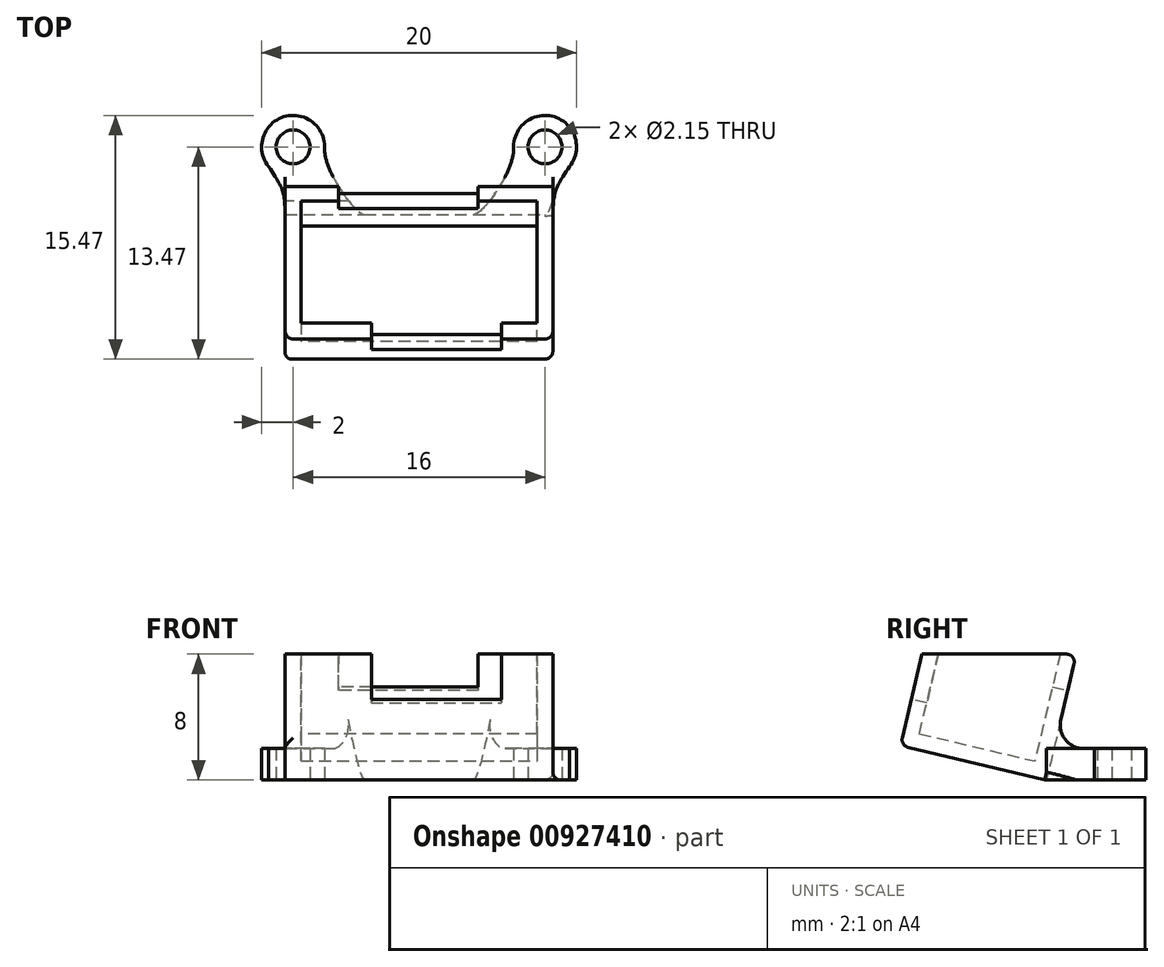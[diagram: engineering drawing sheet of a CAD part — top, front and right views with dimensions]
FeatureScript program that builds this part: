
annotation { "Feature Type Name" : "Feature", "Feature Type Description" : "" }
export const myFeature = defineFeature(function(context is Context, id is Id, definition is map)
    precondition{}
    {
        {
            assignVariable(context, id + "F0", {"name" : "HolderThickness", "anyValue" : 1 * mm});
        }
        {
            assignVariable(context, id + "F1", {"name" : "SpacerThickness", "anyValue" : 2 * mm});
        }
        {
            var Q0;
            Q0=qCreatedBy(makeId("Top.planeOp"),FACE);
            cPlane(context, id + "F2", {"entities" : qUnion([Q0]), "cplaneType" : CPlaneType.OFFSET, "offset" : 15 * mm, "oppositeDirection" : true, "width" : 150 * mm, "height" : 150 * mm});
        }
        {
            var Q0;
            Q0=qCreatedBy(id+"F2.planeOp",FACE);
            cPlane(context, id + "F3", {"entities" : qUnion([Q0]), "cplaneType" : CPlaneType.OFFSET, "offset" : 8 * mm, "width" : 150 * mm, "height" : 150 * mm});
        }
        {
            var Q0;
            Q0=qCreatedBy(id+"F2.planeOp",FACE);
            var sketch = newSketch(context, id + "F4", { "sketchPlane" : qUnion([Q0])});
            skLineSegment(sketch, "E0.bottom", {"start": v(-8.5, -4.3) * mm, "end": v(8.5, -4.3) * mm});
            skLineSegment(sketch, "E0.top", {"start": v(-8.5, -14.1) * mm, "end": v(8.5, -14.1) * mm});
            skLineSegment(sketch, "E0.left", {"start": v(-8.5, -4.3) * mm, "end": v(-8.5, -14.1) * mm});
            skLineSegment(sketch, "E0.right", {"start": v(8.5, -4.3) * mm, "end": v(8.5, -14.1) * mm});
            skPoint(sketch, "E1", {"position": v(0, -4.3) * mm});
            skSolve(sketch);
        }
        {
            var Q0;
            Q0=qCreatedBy(id+"F3.planeOp",FACE);
            var sketch = newSketch(context, id + "F5", { "sketchPlane" : qUnion([Q0])});
            skLineSegment(sketch, "E2.bottom", {"start": v(-8.5, -2.4) * mm, "end": v(8.5, -2.4) * mm});
            skLineSegment(sketch, "E2.top", {"start": v(-8.5, -12.2) * mm, "end": v(8.5, -12.2) * mm});
            skLineSegment(sketch, "E2.left", {"start": v(-8.5, -2.4) * mm, "end": v(-8.5, -12.2) * mm});
            skLineSegment(sketch, "E2.right", {"start": v(8.5, -2.4) * mm, "end": v(8.5, -12.2) * mm});
            skSolve(sketch);
        }
        {
            var Q0;
            Q0=qSketchRegion(id+"F5",true);
            var Q1;
            Q1=qSketchRegion(id+"F4",true);
            loft(context, id + "F6", {"sheetProfilesArray" : [{ "sheetProfileEntities" : qUnion([Q0]) }, { "sheetProfileEntities" : qUnion([Q1]) }]});
        }
        {
            var Q0;
            Q0=makeQuery(id+"F6.opLoft","SWEPT_FACE",FACE,{"disambiguationData":[OSD([sQuery(id+"F4.wireOp",EDGE,"E0.bottom"),sQuery(id+"F4.wireOp",EDGE,"E0.top"),sQuery(id+"F4.wireOp",EDGE,"E0.left"),sQuery(id+"F5.wireOp",EDGE,"E2.bottom"),sQuery(id+"F5.wireOp",EDGE,"E2.top"),sQuery(id+"F5.wireOp",EDGE,"E2.left")])]});
            var sketch = newSketch(context, id + "F7", { "sketchPlane" : qUnion([Q0])});
            skLineSegment(sketch, "E3", {"start": v(4.3, -15) * mm, "end": v(4.07, -14.03) * mm, "construction": true});
            skLineSegment(sketch, "E4", {"start": v(4.3, -15) * mm, "end": v(14.29, -12.63) * mm});
            skLineSegment(sketch, "E5", {"start": v(14.29, -12.63) * mm, "end": v(15.54, -17.9) * mm});
            skLineSegment(sketch, "E6", {"start": v(15.54, -17.9) * mm, "end": v(6.25, -20.1) * mm});
            skLineSegment(sketch, "E7", {"start": v(6.25, -20.1) * mm, "end": v(4.3, -15) * mm});
            skSolve(sketch);
        }
        {
            var Q0;
            Q0=qSketchRegion(id+"F7",true);
            extrude(context, id + "F8", {"entities" : qUnion([Q0]), "operationType" : NewBodyOperationType.REMOVE, "oppositeDirection" : true, "depth" : 25 * mm, "offsetDistance" : 25 * mm});
        }
        {
            var Q0;
            Q0=makeQuery(id+"F6.opLoft","CAP_FACE",FACE,{"disambiguationData":[OSD([makeQuery(id+"F5.imprint","IMPRINT",FACE,{"disambiguationData":[TD([[makeQuery(id+"F5.imprint","IMPRINT",EDGE,{"derivedFrom":sQuery(id+"F5.wireOp",EDGE,"E2.bottom")}),-1.0]])]})])],"isStart":true});
            shell(context, id + "F9", {"entities" : qUnion([Q0]), "thickness" : 1 * mm});
        }
        {
            var Q0;
            Q0=makeQuery(id+"F6.opLoft","SWEPT_FACE",FACE,{"disambiguationData":[OSD([sQuery(id+"F4.wireOp",EDGE,"E0.top"),sQuery(id+"F4.wireOp",EDGE,"E0.left"),sQuery(id+"F4.wireOp",EDGE,"E0.right"),sQuery(id+"F5.wireOp",EDGE,"E2.top"),sQuery(id+"F5.wireOp",EDGE,"E2.left"),sQuery(id+"F5.wireOp",EDGE,"E2.right")])]});
            var sketch = newSketch(context, id + "F10", { "sketchPlane" : qUnion([Q0])});
            skPoint(sketch, "E8.0", {"position": v(-7.5, -14.59) * mm});
            skPoint(sketch, "E9.0", {"position": v(-7.5, -7.6) * mm});
            skPoint(sketch, "E10.0", {"position": v(7.5, -7.6) * mm});
            skPoint(sketch, "E11.0", {"position": v(7.5, -14.59) * mm});
            skLineSegment(sketch, "E12.bottom", {"start": v(-3.02, -4.34) * mm, "end": v(5.23, -4.34) * mm});
            skLineSegment(sketch, "E12.top", {"start": v(-3.03, -12.59) * mm, "end": v(5.23, -12.59) * mm});
            skLineSegment(sketch, "E12.left", {"start": v(-3.02, -4.34) * mm, "end": v(-3.03, -12.59) * mm});
            skLineSegment(sketch, "E12.right", {"start": v(5.23, -4.34) * mm, "end": v(5.23, -12.59) * mm});
            skSolve(sketch);
        }
        {
            var Q0;
            Q0=qSketchRegion(id+"F10",true);
            extrude(context, id + "F11", {"entities" : qUnion([Q0]), "operationType" : NewBodyOperationType.REMOVE, "oppositeDirection" : true, "depth" : getVariable(context, 'HolderThickness'), "offsetDistance" : 25 * mm});
        }
        {
            var Q0;
            Q0=qCreatedBy(id+"F2.planeOp",FACE);
            var sketch = newSketch(context, id + "F12", { "sketchPlane" : qUnion([Q0])});
            skCircle(sketch, "E13", {"center": v(-8, 0) * mm, "radius": 1.07 * mm});
            skCircle(sketch, "E14", {"center": v(8, 0) * mm, "radius": 1.07 * mm});
            skLineSegment(sketch, "E15", {"start": v(8, 0) * mm, "end": v(-8, 0) * mm, "construction": true});
            skCircle(sketch, "E16", {"center": v(-8, 0) * mm, "radius": 2 * mm});
            skCircle(sketch, "E17", {"center": v(8, 0) * mm, "radius": 2 * mm});
            skPoint(sketch, "E18", {"position": v(-9.07, 0) * mm});
            skFitSpline(sketch, "E19.MirrorCS", {"points": [v(-6, -0.14) * mm, v(-3.48, -4.3) * mm], "startDerivative": vector(0, -4.37) * mm, "endDerivative": vector(1.84, -0.2) * mm});
            skFitSpline(sketch, "E20", {"points": [v(-8.5, -4.3) * mm, v(-9.57, -1.24) * mm], "startDerivative": vector(-0.13, 4.25) * mm, "endDerivative": vector(-2.9, 4.1) * mm});
            skLineSegment(sketch, "E21", {"start": v(0, 3.34) * mm, "end": v(0, -3.34) * mm, "construction": true});
            skPoint(sketch, "E21.startSnap0", {"position": v(0, 0) * mm});
            skFitSpline(sketch, "E22.MirrorCS", {"points": [v(6, -0.14) * mm, v(3.48, -4.3) * mm], "startDerivative": vector(0, -4.37) * mm, "endDerivative": vector(-1.84, -0.2) * mm});
            skFitSpline(sketch, "E23.MirrorCS", {"points": [v(8.5, -4.3) * mm, v(9.57, -1.24) * mm], "startDerivative": vector(0.13, 4.25) * mm, "endDerivative": vector(2.9, 4.1) * mm});
            skLineSegment(sketch, "E24", {"start": v(-3.48, -4.3) * mm, "end": v(-8.5, -4.3) * mm});
            skLineSegment(sketch, "E25.MirrorCS", {"start": v(3.48, -4.3) * mm, "end": v(8.5, -4.3) * mm});
            skSolve(sketch);
        }
        {
            var Q0;
            Q0=makeQuery(id+"F12.imprint","IMPRINT",FACE,{"disambiguationData":[TD([[makeQuery(id+"F12.imprint","IMPRINT",EDGE,{"derivedFrom":sQuery(id+"F12.wireOp",EDGE,"E13")}),-1.0]])]});
            var Q1;
            Q1=makeQuery(id+"F12.imprint","IMPRINT",FACE,{"disambiguationData":[TD([[makeQuery(id+"F12.imprint","IMPRINT",EDGE,{"derivedFrom":sQuery(id+"F12.wireOp",EDGE,"E14")}),-1.0]])]});
            extrude(context, id + "F13", {"entities" : qUnion([Q0, Q1]), "depth" : getVariable(context, 'SpacerThickness'), "offsetDistance" : 25 * mm});
        }
        {
            var Q0;
            {var subQ0=sQuery(id+"F12.wireOp",EDGE,"E19.MirrorCS");Q0=makeQuery(id+"F12.imprint","IMPRINT",FACE,{"disambiguationData":[TD([[makeQuery(id+"F12.imprint","IMPRINT",EDGE,{"derivedFrom":subQ0}),-1.0]])]});}
            var Q1;
            {var subQ0=sQuery(id+"F12.wireOp",EDGE,"E22.MirrorCS");Q1=makeQuery(id+"F12.imprint","IMPRINT",FACE,{"disambiguationData":[TD([[makeQuery(id+"F12.imprint","IMPRINT",EDGE,{"derivedFrom":subQ0}),1.0]])]});}
            extrude(context, id + "F14", {"entities" : qUnion([Q0, Q1]), "operationType" : NewBodyOperationType.ADD, "depth" : 2 * mm, "offsetDistance" : 25 * mm});
        }
        {
            var Q0;
            Q0=makeQuery(id+"F14.boolean.opBoolean","INTERSECT",EDGE,{"derivedFrom":[makeQuery(id+"F6.opLoft","SWEPT_FACE",FACE,{"disambiguationData":[OSD([sQuery(id+"F4.wireOp",EDGE,"E0.bottom"),sQuery(id+"F4.wireOp",EDGE,"E0.left"),sQuery(id+"F4.wireOp",EDGE,"E0.right"),sQuery(id+"F5.wireOp",EDGE,"E2.bottom"),sQuery(id+"F5.wireOp",EDGE,"E2.left"),sQuery(id+"F5.wireOp",EDGE,"E2.right")])]}),makeQuery(id+"F14.opExtrude","CAP_FACE",FACE,{"disambiguationData":[OSD([sQuery(id+"F12.wireOp",EDGE,"E17"),sQuery(id+"F12.wireOp",EDGE,"E22.MirrorCS"),sQuery(id+"F12.wireOp",EDGE,"E23.MirrorCS"),sQuery(id+"F12.wireOp",EDGE,"E25.MirrorCS")])],"isStart":false})]});
            var Q1;
            Q1=makeQuery(id+"F14.boolean.opBoolean","INTERSECT",EDGE,{"derivedFrom":[makeQuery(id+"F6.opLoft","SWEPT_FACE",FACE,{"disambiguationData":[OSD([sQuery(id+"F4.wireOp",EDGE,"E0.bottom"),sQuery(id+"F4.wireOp",EDGE,"E0.left"),sQuery(id+"F4.wireOp",EDGE,"E0.right"),sQuery(id+"F5.wireOp",EDGE,"E2.bottom"),sQuery(id+"F5.wireOp",EDGE,"E2.left"),sQuery(id+"F5.wireOp",EDGE,"E2.right")])]}),makeQuery(id+"F14.opExtrude","CAP_FACE",FACE,{"disambiguationData":[OSD([sQuery(id+"F12.wireOp",EDGE,"E16"),sQuery(id+"F12.wireOp",EDGE,"E19.MirrorCS"),sQuery(id+"F12.wireOp",EDGE,"E20"),sQuery(id+"F12.wireOp",EDGE,"E24")])],"isStart":false})]});
            fillet(context, id + "F15", {"entities" : qUnion([Q0, Q1]), "radius" : 1.5 * mm, "tangentPropagation" : true, "allowEdgeOverflow" : false});
        }
        {
            var Q0;
            Q0=makeQuery(id+"F13.boolean.opBoolean","INTERSECT",EDGE,{"derivedFrom":[makeQuery(id+"F6.opLoft","SWEPT_FACE",FACE,{"disambiguationData":[OSD([sQuery(id+"F4.wireOp",EDGE,"E0.bottom"),sQuery(id+"F4.wireOp",EDGE,"E0.top"),sQuery(id+"F4.wireOp",EDGE,"E0.right"),sQuery(id+"F5.wireOp",EDGE,"E2.bottom"),sQuery(id+"F5.wireOp",EDGE,"E2.top"),sQuery(id+"F5.wireOp",EDGE,"E2.right")])]}),makeQuery(id+"F13.opExtrude","CAP_FACE",FACE,{"disambiguationData":[OSD([sQuery(id+"F12.wireOp",EDGE,"E14"),sQuery(id+"F12.wireOp",EDGE,"E17"),sQuery(id+"F12.wireOp",EDGE,"E22.MirrorCS"),sQuery(id+"F12.wireOp",EDGE,"E23.MirrorCS"),sQuery(id+"F12.wireOp",EDGE,"E25.MirrorCS")])],"isStart":false})]});
            var Q1;
            Q1=makeQuery(id+"F13.boolean.opBoolean","INTERSECT",EDGE,{"derivedFrom":[makeQuery(id+"F6.opLoft","SWEPT_FACE",FACE,{"disambiguationData":[OSD([sQuery(id+"F4.wireOp",EDGE,"E0.bottom"),sQuery(id+"F4.wireOp",EDGE,"E0.top"),sQuery(id+"F4.wireOp",EDGE,"E0.left"),sQuery(id+"F5.wireOp",EDGE,"E2.bottom"),sQuery(id+"F5.wireOp",EDGE,"E2.top"),sQuery(id+"F5.wireOp",EDGE,"E2.left")])]}),makeQuery(id+"F13.opExtrude","CAP_FACE",FACE,{"disambiguationData":[OSD([sQuery(id+"F12.wireOp",EDGE,"E13"),sQuery(id+"F12.wireOp",EDGE,"E16"),sQuery(id+"F12.wireOp",EDGE,"E19.MirrorCS"),sQuery(id+"F12.wireOp",EDGE,"E20"),sQuery(id+"F12.wireOp",EDGE,"E24")])],"isStart":false})]});
            var Q2;
            Q2=makeQuery(id+"F6.opLoft","MID_CAP_EDGE",EDGE,{"disambiguationData":[OSD([sQuery(id+"F5.wireOp",EDGE,"E2.bottom"),sQuery(id+"F5.wireOp",EDGE,"E2.left"),sQuery(id+"F5.wireOp",EDGE,"E2.right")])],"capPos":0.0});
            var Q3;
            Q3=makeQuery(id+"F8.boolean.opBoolean","INTERSECT",EDGE,{"derivedFrom":[makeQuery(id+"F6.opLoft","SWEPT_FACE",FACE,{"disambiguationData":[OSD([sQuery(id+"F4.wireOp",EDGE,"E0.top"),sQuery(id+"F4.wireOp",EDGE,"E0.left"),sQuery(id+"F4.wireOp",EDGE,"E0.right"),sQuery(id+"F5.wireOp",EDGE,"E2.top"),sQuery(id+"F5.wireOp",EDGE,"E2.left"),sQuery(id+"F5.wireOp",EDGE,"E2.right")])]}),makeQuery(id+"F8.opExtrude","SWEPT_FACE",FACE,{"disambiguationData":[OSD([sQuery(id+"F7.wireOp",EDGE,"E4")])]})]});
            var Q4;
            Q4=makeQuery(id+"F6.opLoft","SWEPT_EDGE",EDGE,{"disambiguationData":[OSD([sQuery(id+"F4.wireOp",EDGE,"E0.top"),sQuery(id+"F4.wireOp",EDGE,"E0.right"),sQuery(id+"F5.wireOp",EDGE,"E2.top"),sQuery(id+"F5.wireOp",EDGE,"E2.right")])]});
            var Q5;
            Q5=makeQuery(id+"F8.boolean.opBoolean","INTERSECT",EDGE,{"derivedFrom":[makeQuery(id+"F6.opLoft","SWEPT_FACE",FACE,{"disambiguationData":[OSD([sQuery(id+"F4.wireOp",EDGE,"E0.bottom"),sQuery(id+"F4.wireOp",EDGE,"E0.top"),sQuery(id+"F4.wireOp",EDGE,"E0.right"),sQuery(id+"F5.wireOp",EDGE,"E2.bottom"),sQuery(id+"F5.wireOp",EDGE,"E2.top"),sQuery(id+"F5.wireOp",EDGE,"E2.right")])]}),makeQuery(id+"F8.opExtrude","SWEPT_FACE",FACE,{"disambiguationData":[OSD([sQuery(id+"F7.wireOp",EDGE,"E4")])]})]});
            var Q6;
            Q6=makeQuery(id+"F8.boolean.opBoolean","COPY",EDGE,{"derivedFrom":makeQuery(id+"F8.opExtrude","CAP_EDGE",EDGE,{"disambiguationData":[OSD([sQuery(id+"F7.wireOp",EDGE,"E4")])],"isStart":true})});
            var Q7;
            Q7=makeQuery(id+"F6.opLoft","SWEPT_EDGE",EDGE,{"disambiguationData":[OSD([sQuery(id+"F4.wireOp",EDGE,"E0.top"),sQuery(id+"F4.wireOp",EDGE,"E0.left"),sQuery(id+"F5.wireOp",EDGE,"E2.top"),sQuery(id+"F5.wireOp",EDGE,"E2.left")])]});
            fillet(context, id + "F16", {"entities" : qUnion([Q0, Q1, Q2, Q3, Q4, Q5, Q6, Q7]), "radius" : 0.5 * mm, "tangentPropagation" : true, "allowEdgeOverflow" : false});
        }
        {
            var Q0;
            Q0=makeQuery(id+"F6.opLoft","SWEPT_FACE",FACE,{"disambiguationData":[OSD([sQuery(id+"F4.wireOp",EDGE,"E0.bottom"),sQuery(id+"F4.wireOp",EDGE,"E0.left"),sQuery(id+"F4.wireOp",EDGE,"E0.right"),sQuery(id+"F5.wireOp",EDGE,"E2.bottom"),sQuery(id+"F5.wireOp",EDGE,"E2.left"),sQuery(id+"F5.wireOp",EDGE,"E2.right")])]});
            var sketch = newSketch(context, id + "F17", { "sketchPlane" : qUnion([Q0])});
            skLineSegment(sketch, "E26.0", {"start": v(7.5, -14.59) * mm, "end": v(-7.5, -14.59) * mm, "construction": true});
            skLineSegment(sketch, "E27", {"start": v(-3.75, -9.74) * mm, "end": v(5.1, -9.74) * mm});
            skLineSegment(sketch, "E28.0", {"start": v(7.5, -7.6) * mm, "end": v(7.5, -14.59) * mm, "construction": true});
            skLineSegment(sketch, "E29.0", {"start": v(-7.5, -7.6) * mm, "end": v(-7.5, -14.59) * mm, "construction": true});
            skLineSegment(sketch, "E30", {"start": v(5.1, -9.74) * mm, "end": v(5.1, -6.6) * mm});
            skLineSegment(sketch, "E31", {"start": v(5.1, -6.6) * mm, "end": v(-3.75, -6.6) * mm});
            skLineSegment(sketch, "E32", {"start": v(-3.75, -6.6) * mm, "end": v(-3.75, -9.74) * mm});
            skSolve(sketch);
        }
        {
            var Q0;
            Q0=qSketchRegion(id+"F17",true);
            extrude(context, id + "F18", {"entities" : qUnion([Q0]), "operationType" : NewBodyOperationType.REMOVE, "oppositeDirection" : true, "depth" : 3 * mm, "offsetDistance" : 25 * mm});
        }
    });
